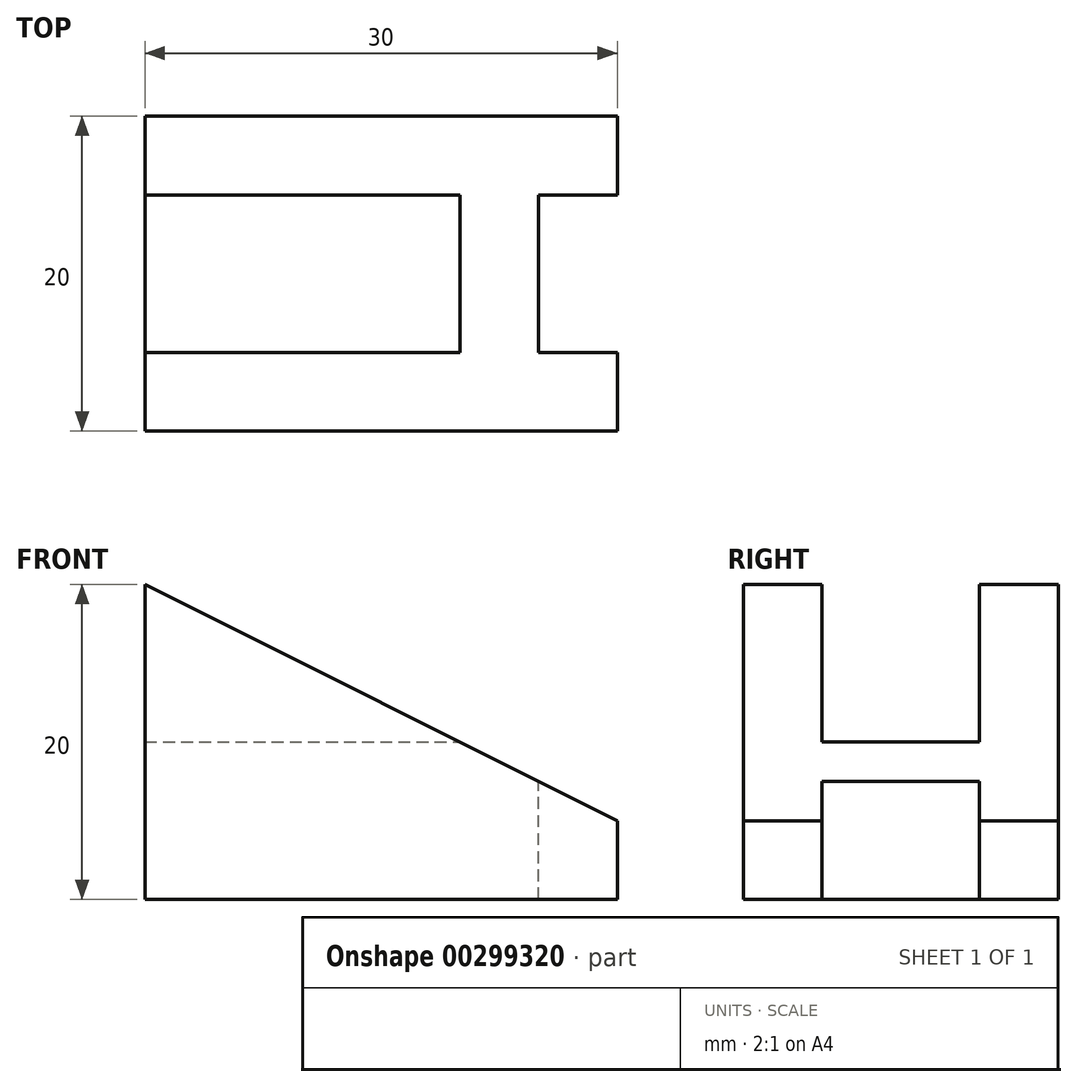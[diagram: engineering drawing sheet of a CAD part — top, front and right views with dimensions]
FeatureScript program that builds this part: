
annotation { "Feature Type Name" : "Feature", "Feature Type Description" : "" }
export const myFeature = defineFeature(function(context is Context, id is Id, definition is map)
    precondition{}
    {
        {
            var Q0;
            Q0=qCreatedBy(makeId("Top.planeOp"),FACE);
            var sketch = newSketch(context, id + "F0", { "sketchPlane" : qUnion([Q0])});
            skLineSegment(sketch, "E0.bottom", {"start": v(0, 0) * mm, "end": v(30, 0) * mm});
            skLineSegment(sketch, "E0.top", {"start": v(0, 20) * mm, "end": v(30, 20) * mm});
            skLineSegment(sketch, "E0.left", {"start": v(0, 0) * mm, "end": v(0, 20) * mm});
            skLineSegment(sketch, "E0.right", {"start": v(30, 0) * mm, "end": v(30, 20) * mm});
            skSolve(sketch);
        }
        {
            var Q0;
            Q0 = qSketchRegion(id + "F0", true);
            extrude(context, id + "F1", {"entities" : qUnion([Q0]), "depth" : 20 * mm});
        }
        {
            var Q0;
            Q0=makeQuery(id+"F1.opExtrude","CAP_FACE",FACE,{"disambiguationData":[OSD([sQuery(id+"F0.wireOp",EDGE,"E0.bottom"),sQuery(id+"F0.wireOp",EDGE,"E0.top"),sQuery(id+"F0.wireOp",EDGE,"E0.left"),sQuery(id+"F0.wireOp",EDGE,"E0.right")])],"isStart":false});
            var sketch = newSketch(context, id + "F2", { "sketchPlane" : qUnion([Q0])});
            skLineSegment(sketch, "E1.bottom", {"start": v(30, 15) * mm, "end": v(25, 15) * mm});
            skLineSegment(sketch, "E1.top", {"start": v(30, 5) * mm, "end": v(25, 5) * mm});
            skLineSegment(sketch, "E1.left", {"start": v(30, 15) * mm, "end": v(30, 5) * mm});
            skLineSegment(sketch, "E1.right", {"start": v(25, 15) * mm, "end": v(25, 5) * mm});
            skSolve(sketch);
        }
        {
            var Q0;
            Q0 = qSketchRegion(id + "F2", true);
            extrude(context, id + "F3", {"entities" : qUnion([Q0]), "operationType" : NewBodyOperationType.REMOVE, "endBound" : BoundingType.THROUGH_ALL, "oppositeDirection" : true, "depth" : 25 * mm});
        }
        {
            var Q0;
            Q0=makeQuery(id+"F1.opExtrude","CAP_FACE",FACE,{"disambiguationData":[OSD([sQuery(id+"F0.wireOp",EDGE,"E0.bottom"),sQuery(id+"F0.wireOp",EDGE,"E0.top"),sQuery(id+"F0.wireOp",EDGE,"E0.left"),sQuery(id+"F0.wireOp",EDGE,"E0.right")])],"isStart":false});
            var sketch = newSketch(context, id + "F4", { "sketchPlane" : qUnion([Q0])});
            skLineSegment(sketch, "E2.bottom", {"start": v(0, 15) * mm, "end": v(20, 15) * mm});
            skLineSegment(sketch, "E2.top", {"start": v(0, 5) * mm, "end": v(20, 5) * mm});
            skLineSegment(sketch, "E2.left", {"start": v(0, 15) * mm, "end": v(0, 5) * mm});
            skLineSegment(sketch, "E2.right", {"start": v(20, 15) * mm, "end": v(20, 5) * mm});
            skSolve(sketch);
        }
        {
            var Q0;
            Q0 = qSketchRegion(id + "F4", true);
            extrude(context, id + "F5", {"entities" : qUnion([Q0]), "operationType" : NewBodyOperationType.REMOVE, "oppositeDirection" : true, "depth" : 10 * mm});
        }
        {
            var Q0;
            Q0=makeQuery(id+"F1.opExtrude","SWEPT_FACE",FACE,{"disambiguationData":[OSD([sQuery(id+"F0.wireOp",EDGE,"E0.bottom")])]});
            var sketch = newSketch(context, id + "F6", { "sketchPlane" : qUnion([Q0])});
            skLineSegment(sketch, "E3", {"start": v(30, 0) * mm, "end": v(30, 5) * mm, "construction": true});
            skLineSegment(sketch, "E4", {"start": v(0, 20) * mm, "end": v(30, 5) * mm});
            skSolve(sketch);
        }
        {
            var Q0;
            {var subQ0=sQuery(id+"F6.wireOp",EDGE,"E4");Q0=makeQuery(id+"F6.imprint","IMPRINT",FACE,{"disambiguationData":[TD([[makeQuery(id+"F6.imprint","IMPRINT",EDGE,{"derivedFrom":subQ0}),1.0]])]});}
            extrude(context, id + "F7", {"entities" : qUnion([Q0]), "operationType" : NewBodyOperationType.REMOVE, "endBound" : BoundingType.THROUGH_ALL, "oppositeDirection" : true, "depth" : 25 * mm});
        }
    });
